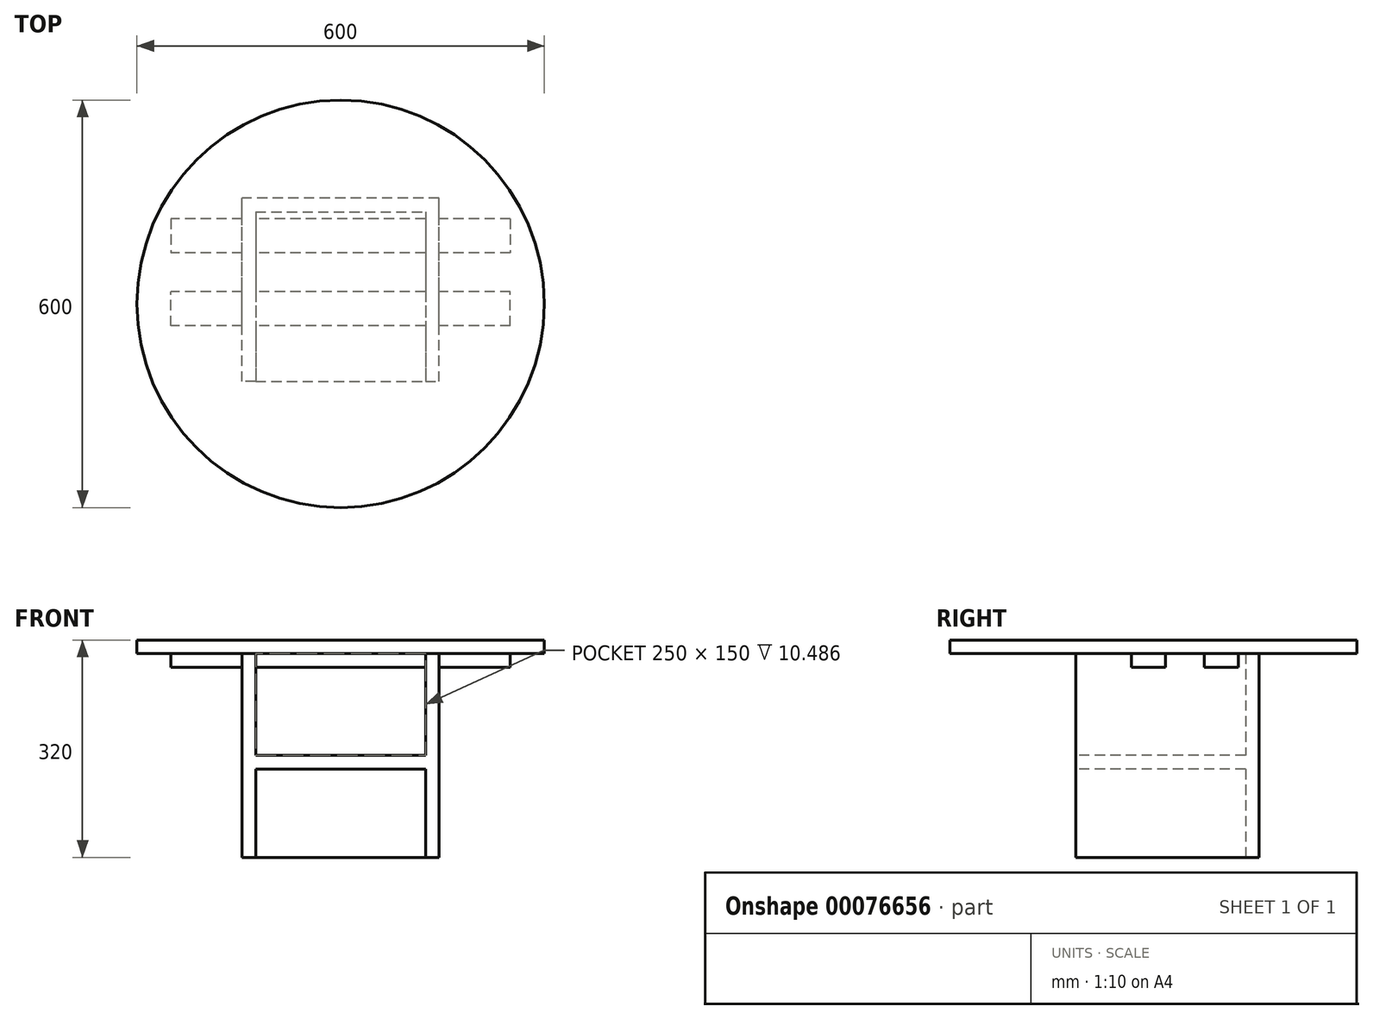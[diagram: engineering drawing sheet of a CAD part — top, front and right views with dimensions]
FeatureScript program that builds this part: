
annotation { "Feature Type Name" : "Feature", "Feature Type Description" : "" }
export const myFeature = defineFeature(function(context is Context, id is Id, definition is map)
    precondition{}
    {
        {
            var Q0;
            Q0=qCreatedBy(makeId("Top.planeOp"),FACE);
            var sketch = newSketch(context, id + "F0", { "sketchPlane" : qUnion([Q0])});
            skLineSegment(sketch, "E0.bottom", {"start": v(-125, 125) * mm, "end": v(125, 125) * mm});
            skLineSegment(sketch, "E0.top", {"start": v(-125, -125) * mm, "end": v(125, -125) * mm});
            skLineSegment(sketch, "E0.left", {"start": v(-125, 125) * mm, "end": v(-125, -125) * mm});
            skLineSegment(sketch, "E0.right", {"start": v(125, 125) * mm, "end": v(125, -125) * mm});
            skPoint(sketch, "E0.middle", {"position": v(0, 0) * mm});
            skSolve(sketch);
        }
        {
            var Q0;
            Q0=makeQuery(id+"F0.imprint","IMPRINT",FACE,{"disambiguationData":[TD([[makeQuery(id+"F0.imprint","IMPRINT",EDGE,{"derivedFrom":sQuery(id+"F0.wireOp",EDGE,"E0.bottom")}),-1.0]])]});
            extrude(context, id + "F1", {"entities" : qUnion([Q0]), "depth" : 20 * mm});
        }
        {
            var Q0;
            Q0=makeQuery(id+"F1.opExtrude","CAP_FACE",FACE,{"disambiguationData":[OSD([sQuery(id+"F0.wireOp",EDGE,"E0.bottom"),sQuery(id+"F0.wireOp",EDGE,"E0.top"),sQuery(id+"F0.wireOp",EDGE,"E0.left"),sQuery(id+"F0.wireOp",EDGE,"E0.right")])],"isStart":false});
            var sketch = newSketch(context, id + "F2", { "sketchPlane" : qUnion([Q0])});
            skLineSegment(sketch, "E1.bottom", {"start": v(-125, -125) * mm, "end": v(-145, -125) * mm});
            skLineSegment(sketch, "E1.top", {"start": v(-125, 145) * mm, "end": v(-145, 145) * mm});
            skLineSegment(sketch, "E1.left", {"start": v(-125, -125) * mm, "end": v(-125, 145) * mm});
            skLineSegment(sketch, "E1.right", {"start": v(-145, -125) * mm, "end": v(-145, 145) * mm});
            skLineSegment(sketch, "E2.bottom", {"start": v(125, -125) * mm, "end": v(145, -125) * mm});
            skLineSegment(sketch, "E2.top", {"start": v(125, 145) * mm, "end": v(145, 145) * mm});
            skLineSegment(sketch, "E2.left", {"start": v(125, -125) * mm, "end": v(125, 145) * mm});
            skLineSegment(sketch, "E2.right", {"start": v(145, -125) * mm, "end": v(145, 145) * mm});
            skLineSegment(sketch, "E3.bottom", {"start": v(-135, 145) * mm, "end": v(134.55, 145) * mm});
            skLineSegment(sketch, "E3.top", {"start": v(-135, 125) * mm, "end": v(134.55, 125) * mm});
            skLineSegment(sketch, "E3.left", {"start": v(-135, 145) * mm, "end": v(-135, 125) * mm});
            skLineSegment(sketch, "E3.right", {"start": v(134.55, 145) * mm, "end": v(134.55, 125) * mm});
            skSolve(sketch);
        }
        {
            var Q0;
            {var subQ4=sQuery(id+"F2.wireOp",EDGE,"E1.bottom");Q0=makeQuery(id+"F2.imprint","IMPRINT",FACE,{"disambiguationData":[TD([[makeQuery(id+"F2.imprint","IMPRINT",EDGE,{"derivedFrom":subQ4}),-1.0]])]});}
            var Q1;
            {var subQ5=sQuery(id+"F2.wireOp",EDGE,"E3.left");Q1=makeQuery(id+"F2.imprint","IMPRINT",FACE,{"disambiguationData":[TD([[makeQuery(id+"F2.imprint","IMPRINT",EDGE,{"derivedFrom":subQ5}),1.0]])]});}
            var Q2;
            {var subQ1=sQuery(id+"F2.wireOp",EDGE,"E1.left");var subQ3=sQuery(id+"F2.wireOp",EDGE,"E3.bottom");var subQ4=makeQuery(id+"F2.imprint","INTERSECT",VERTEX,{"derivedFrom":[subQ1,subQ3]});Q2=makeQuery(id+"F2.imprint","IMPRINT",FACE,{"disambiguationData":[TD([[makeQuery(id+"F2.imprint","IMPRINT",EDGE,{"disambiguationData":[TD([[subQ4,1.0]])],"derivedFrom":subQ1}),-1.0]])]});}
            var Q3;
            {var subQ5=sQuery(id+"F2.wireOp",EDGE,"E3.right");Q3=makeQuery(id+"F2.imprint","IMPRINT",FACE,{"disambiguationData":[TD([[makeQuery(id+"F2.imprint","IMPRINT",EDGE,{"derivedFrom":subQ5}),-1.0]])]});}
            var Q4;
            {var subQ3=sQuery(id+"F2.wireOp",EDGE,"E2.bottom");Q4=makeQuery(id+"F2.imprint","IMPRINT",FACE,{"disambiguationData":[TD([[makeQuery(id+"F2.imprint","IMPRINT",EDGE,{"derivedFrom":subQ3}),1.0]])]});}
            extrude(context, id + "F3", {"entities" : qUnion([Q0, Q1, Q2, Q3, Q4]), "operationType" : NewBodyOperationType.ADD, "endBound" : BoundingType.SYMMETRIC, "depth" : 300 * mm});
        }
        {
            var Q0;
            Q0=makeQuery(id+"F3.opExtrude","CAP_FACE",FACE,{"disambiguationData":[OSD([sQuery(id+"F2.wireOp",EDGE,"E1.bottom"),sQuery(id+"F2.wireOp",EDGE,"E1.top"),sQuery(id+"F2.wireOp",EDGE,"E1.left"),sQuery(id+"F2.wireOp",EDGE,"E1.right"),sQuery(id+"F2.wireOp",EDGE,"E2.bottom"),sQuery(id+"F2.wireOp",EDGE,"E2.top"),sQuery(id+"F2.wireOp",EDGE,"E2.left"),sQuery(id+"F2.wireOp",EDGE,"E2.right"),sQuery(id+"F2.wireOp",EDGE,"E3.bottom"),sQuery(id+"F2.wireOp",EDGE,"E3.top")])],"isStart":false});
            var sketch = newSketch(context, id + "F4", { "sketchPlane" : qUnion([Q0])});
            skLineSegment(sketch, "E4.bottom", {"start": v(250, 114.51) * mm, "end": v(-250, 114.51) * mm});
            skLineSegment(sketch, "E4.top", {"start": v(250, 64.51) * mm, "end": v(-250, 64.51) * mm});
            skLineSegment(sketch, "E4.left", {"start": v(250, 114.51) * mm, "end": v(250, 64.51) * mm});
            skLineSegment(sketch, "E4.right", {"start": v(-250, 114.51) * mm, "end": v(-250, 64.51) * mm});
            skPoint(sketch, "E4.middle", {"position": v(0, 89.51) * mm});
            skPoint(sketch, "E4.middle.positionSnap0", {"position": v(0, 125) * mm});
            skPoint(sketch, "E4.centerSnap0", {"position": v(0, 125) * mm});
            skLineSegment(sketch, "E5.bottom", {"start": v(250, -43.02) * mm, "end": v(-250, -43.02) * mm});
            skLineSegment(sketch, "E5.top", {"start": v(250, 6.98) * mm, "end": v(-250, 6.98) * mm});
            skLineSegment(sketch, "E5.left", {"start": v(250, -43.02) * mm, "end": v(250, 6.98) * mm});
            skLineSegment(sketch, "E5.right", {"start": v(-250, -43.02) * mm, "end": v(-250, 6.98) * mm});
            skPoint(sketch, "E5.middle", {"position": v(0, -18.02) * mm});
            skSolve(sketch);
        }
        {
            var Q0;
            {var subQ0=sQuery(id+"F4.wireOp",EDGE,"E4.right");Q0=makeQuery(id+"F4.imprint","IMPRINT",FACE,{"disambiguationData":[TD([[makeQuery(id+"F4.imprint","IMPRINT",EDGE,{"derivedFrom":subQ0}),1.0]])]});}
            var Q1;
            {var subQ0=sQuery(id+"F4.wireOp",EDGE,"E5.right");Q1=makeQuery(id+"F4.imprint","IMPRINT",FACE,{"disambiguationData":[TD([[makeQuery(id+"F4.imprint","IMPRINT",EDGE,{"derivedFrom":subQ0}),-1.0]])]});}
            var Q2;
            {var subQ0=sQuery(id+"F4.wireOp",EDGE,"E5.bottom");var subQ1=makeQuery(id+"F3.opExtrude","CAP_EDGE",EDGE,{"disambiguationData":[OSD([sQuery(id+"F2.wireOp",EDGE,"E2.left")])],"isStart":false});var subQ2=makeQuery(id+"F4.imprint","INTERSECT",VERTEX,{"derivedFrom":[subQ1,subQ0]});Q2=makeQuery(id+"F4.imprint","IMPRINT",FACE,{"disambiguationData":[TD([[makeQuery(id+"F4.imprint","IMPRINT",EDGE,{"disambiguationData":[TD([[subQ2,-1.0]])],"derivedFrom":subQ0}),-1.0]])]});}
            var Q3;
            {var subQ0=sQuery(id+"F4.wireOp",EDGE,"E4.bottom");var subQ1=makeQuery(id+"F3.opExtrude","CAP_EDGE",EDGE,{"disambiguationData":[OSD([sQuery(id+"F2.wireOp",EDGE,"E2.left")])],"isStart":false});var subQ2=makeQuery(id+"F4.imprint","INTERSECT",VERTEX,{"derivedFrom":[subQ1,subQ0]});Q3=makeQuery(id+"F4.imprint","IMPRINT",FACE,{"disambiguationData":[TD([[makeQuery(id+"F4.imprint","IMPRINT",EDGE,{"disambiguationData":[TD([[subQ2,-1.0]])],"derivedFrom":subQ0}),1.0]])]});}
            var Q4;
            {var subQ0=sQuery(id+"F4.wireOp",EDGE,"E4.left");Q4=makeQuery(id+"F4.imprint","IMPRINT",FACE,{"disambiguationData":[TD([[makeQuery(id+"F4.imprint","IMPRINT",EDGE,{"derivedFrom":subQ0}),-1.0]])]});}
            var Q5;
            {var subQ0=sQuery(id+"F4.wireOp",EDGE,"E5.left");Q5=makeQuery(id+"F4.imprint","IMPRINT",FACE,{"disambiguationData":[TD([[makeQuery(id+"F4.imprint","IMPRINT",EDGE,{"derivedFrom":subQ0}),1.0]])]});}
            extrude(context, id + "F5", {"entities" : qUnion([Q0, Q1, Q2, Q3, Q4, Q5]), "operationType" : NewBodyOperationType.ADD, "oppositeDirection" : true, "depth" : 20 * mm});
        }
        {
            var Q0;
            {var subQ0=sQuery(id+"F4.wireOp",EDGE,"E5.top");var subQ1=sQuery(id+"F4.wireOp",EDGE,"E5.bottom");var subQ2=sQuery(id+"F2.wireOp",EDGE,"E1.right");var subQ3=sQuery(id+"F2.wireOp",EDGE,"E2.left");var subQ4=sQuery(id+"F2.wireOp",EDGE,"E1.left");var subQ5=sQuery(id+"F2.wireOp",EDGE,"E2.right");var subQ6=sQuery(id+"F4.wireOp",EDGE,"E4.top");var subQ7=sQuery(id+"F4.wireOp",EDGE,"E4.bottom");Q0=makeQuery(id+"F5.boolean.opBoolean","MERGE",FACE,{"derivedFrom":[makeQuery(id+"F3.opExtrude","CAP_FACE",FACE,{"disambiguationData":[OSD([sQuery(id+"F2.wireOp",EDGE,"E1.bottom"),sQuery(id+"F2.wireOp",EDGE,"E1.top"),subQ4,subQ2,sQuery(id+"F2.wireOp",EDGE,"E2.bottom"),sQuery(id+"F2.wireOp",EDGE,"E2.top"),subQ3,subQ5,sQuery(id+"F2.wireOp",EDGE,"E3.bottom"),sQuery(id+"F2.wireOp",EDGE,"E3.top")])],"isStart":false}),makeQuery(id+"F5.opExtrude","CAP_FACE",FACE,{"disambiguationData":[OSD([subQ5,subQ7,subQ6,sQuery(id+"F4.wireOp",EDGE,"E4.left")])],"isStart":true}),makeQuery(id+"F5.opExtrude","CAP_FACE",FACE,{"disambiguationData":[OSD([subQ4,subQ3,subQ7,subQ6])],"isStart":true}),makeQuery(id+"F5.opExtrude","CAP_FACE",FACE,{"disambiguationData":[OSD([subQ2,subQ7,subQ6,sQuery(id+"F4.wireOp",EDGE,"E4.right")])],"isStart":true}),makeQuery(id+"F5.opExtrude","CAP_FACE",FACE,{"disambiguationData":[OSD([subQ5,subQ1,subQ0,sQuery(id+"F4.wireOp",EDGE,"E5.left")])],"isStart":true}),makeQuery(id+"F5.opExtrude","CAP_FACE",FACE,{"disambiguationData":[OSD([subQ4,subQ3,subQ1,subQ0])],"isStart":true}),makeQuery(id+"F5.opExtrude","CAP_FACE",FACE,{"disambiguationData":[OSD([subQ2,subQ1,subQ0,sQuery(id+"F4.wireOp",EDGE,"E5.right")])],"isStart":true})]});}
            cPlane(context, id + "F6", {"entities" : qUnion([Q0]), "cplaneType" : CPlaneType.OFFSET, "offset" : 20 * mm, "width" : 150 * mm, "height" : 150 * mm});
        }
        {
            var Q0;
            Q0=qCreatedBy(id+"F6.planeOp",FACE);
            var sketch = newSketch(context, id + "F7", { "sketchPlane" : qUnion([Q0])});
            skCircle(sketch, "E6", {"center": v(0, -10.6) * mm, "radius": 300 * mm});
            skSolve(sketch);
        }
        {
            var Q0;
            Q0=makeQuery(id+"F7.imprint","IMPRINT",FACE,{"disambiguationData":[TD([[makeQuery(id+"F7.imprint","IMPRINT",EDGE,{"derivedFrom":sQuery(id+"F7.wireOp",EDGE,"E6")}),1.0]])]});
            extrude(context, id + "F8", {"entities" : qUnion([Q0]), "operationType" : NewBodyOperationType.ADD, "oppositeDirection" : true, "depth" : 20 * mm});
        }
    });
